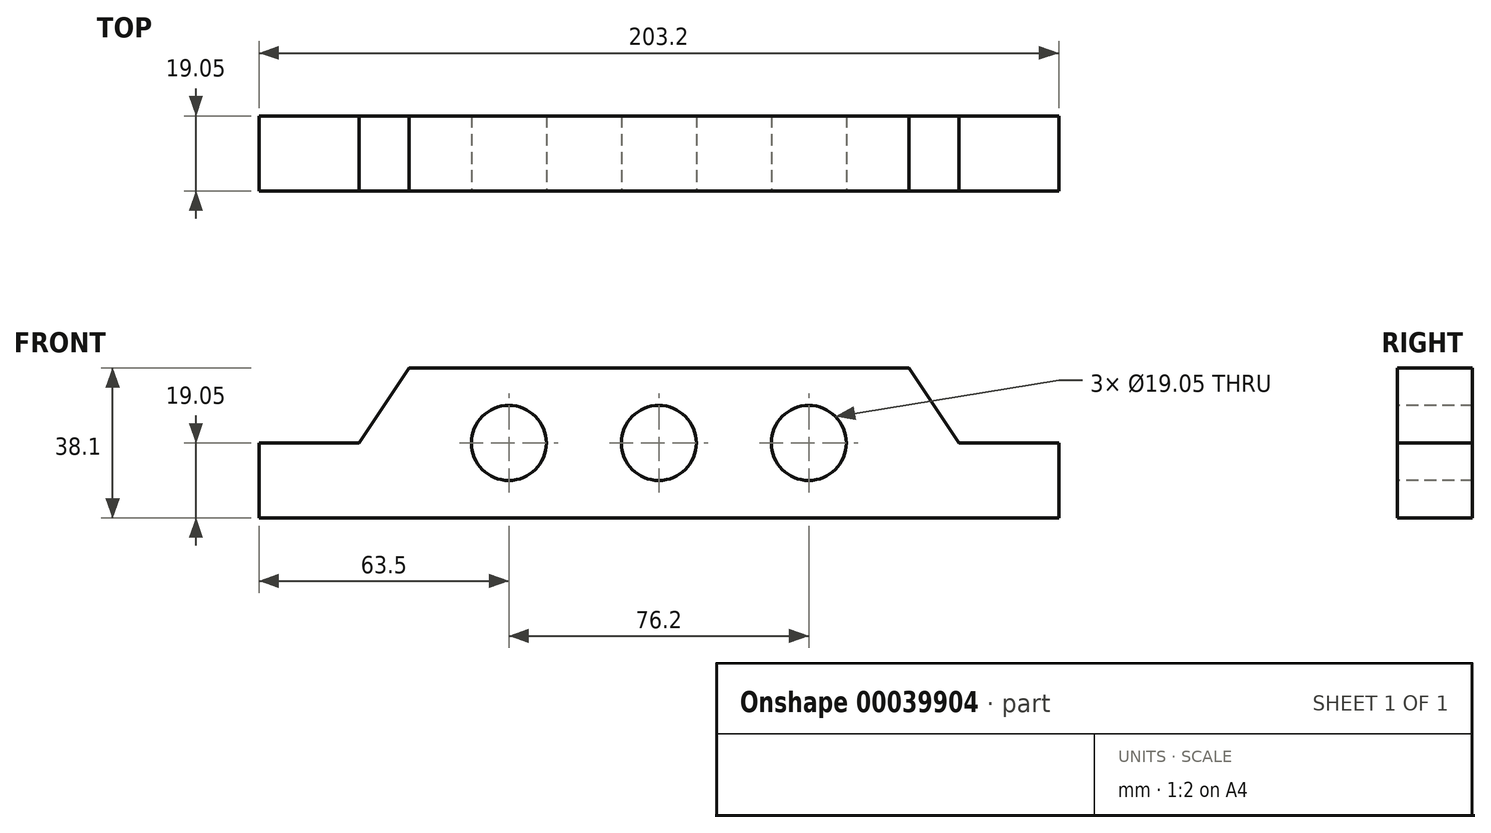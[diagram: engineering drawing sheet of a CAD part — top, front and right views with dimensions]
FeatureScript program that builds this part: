
annotation { "Feature Type Name" : "Feature", "Feature Type Description" : "" }
export const myFeature = defineFeature(function(context is Context, id is Id, definition is map)
    precondition{}
    {
        {
            var Q0;
            Q0=qCreatedBy(makeId("Front.planeOp"),FACE);
            var sketch = newSketch(context, id + "F0", { "sketchPlane" : qUnion([Q0])});
            skLineSegment(sketch, "E0.bottom", {"start": v(-96.52, 0) * mm, "end": v(106.68, 0) * mm});
            skLineSegment(sketch, "E0.top", {"start": v(-58.42, 38.1) * mm, "end": v(68.58, 38.1) * mm});
            skLineSegment(sketch, "E0.left", {"start": v(-96.52, 0) * mm, "end": v(-96.52, 19.05) * mm});
            skLineSegment(sketch, "E0.right", {"start": v(106.68, 0) * mm, "end": v(106.68, 19.05) * mm});
            skLineSegment(sketch, "E1", {"start": v(-96.52, 19.05) * mm, "end": v(-71.12, 19.05) * mm});
            skCircle(sketch, "E2", {"center": v(5.08, 19.05) * mm, "radius": 9.53 * mm});
            skCircle(sketch, "E3", {"center": v(-33.02, 19.05) * mm, "radius": 9.53 * mm});
            skLineSegment(sketch, "E4", {"start": v(-58.42, 38.1) * mm, "end": v(-71.12, 19.05) * mm});
            skLineSegment(sketch, "E5", {"start": v(68.58, 38.1) * mm, "end": v(81.28, 19.05) * mm});
            skCircle(sketch, "E6", {"center": v(43.18, 19.05) * mm, "radius": 9.53 * mm});
            skPoint(sketch, "E7.orphan", {"position": v(-96.52, 38.1) * mm});
            skPoint(sketch, "E8.orphan", {"position": v(106.68, 38.1) * mm});
            skPoint(sketch, "E9.trimOffspring.end.orphan", {"position": v(5.08, 38.1) * mm});
            skPoint(sketch, "E10.start.orphan", {"position": v(5.08, 0) * mm});
            skLineSegment(sketch, "E11.trimOffspring", {"start": v(81.28, 19.05) * mm, "end": v(106.68, 19.05) * mm});
            skSolve(sketch);
        }
        {
            var Q0;
            Q0=makeQuery(id+"F0.imprint","IMPRINT",FACE,{"disambiguationData":[TD([[makeQuery(id+"F0.imprint","IMPRINT",EDGE,{"derivedFrom":sQuery(id+"F0.wireOp",EDGE,"E0.bottom")}),1.0]])]});
            extrude(context, id + "F1", {"entities" : qUnion([Q0]), "oppositeDirection" : true, "depth" : 19.05 * mm});
        }
    });
